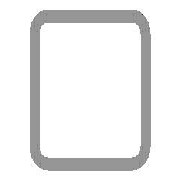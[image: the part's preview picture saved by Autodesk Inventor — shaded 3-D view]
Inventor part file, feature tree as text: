
AUTODESK INVENTOR PART (.ipt)
format: ipt  version: 2025 (Build 290162010, 162A)  size: 133,632 bytes
history: native  units: mm (DEFAULTED — no unit token found)
features: other x4, sketch x1, plane x1
ambient origin geometry x8: Origin, YZ Plane, XZ Plane, XY Plane, X Axis, Y Axis, Z Axis, Center Point
bodies: Solid1 (feature_tree), Body (feature_tree)
feature tree (6):
  parser-record x1  (decoder bookkeeping rows leaked as tree rows — omitted from the tree; the rows remain in map.json)
  other  "Driven Length"
  other  "Start Plane"
  other  "End Plane"
  sketch  "Sketch3"  dims[d3=4410.0mm d4=0.0mm d7=6.0mm d9=80.0mm d11=80.0mm d12=3.0mm d13=-0.0mm d14=4410.0mm d15=40.0mm d16=40.0mm d17=90.0deg d18=4410.0mm]
  plane  "Work Plane3"
